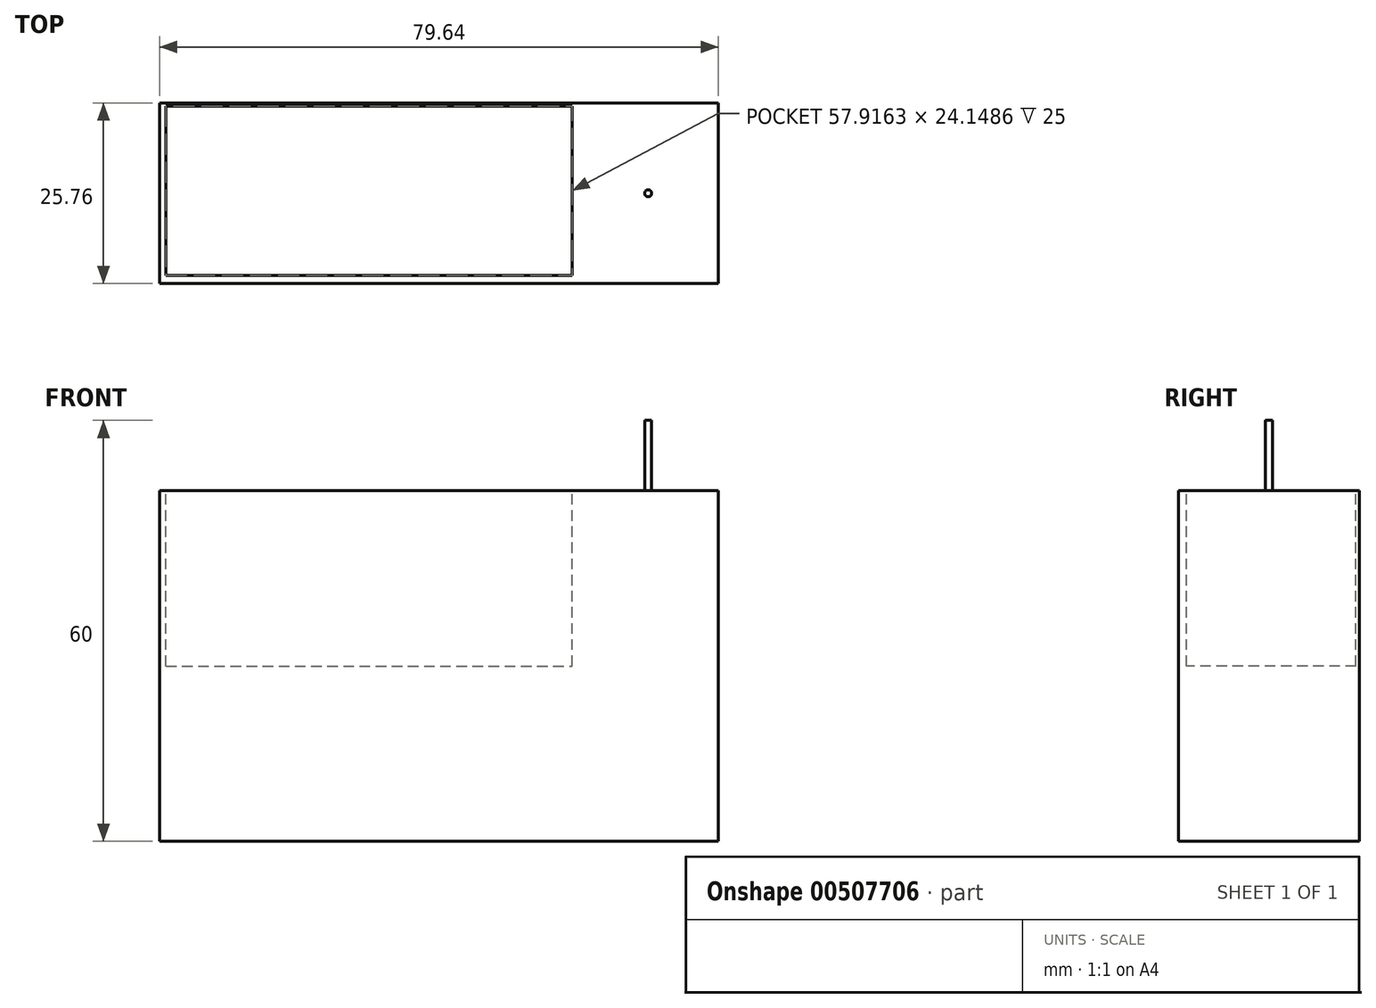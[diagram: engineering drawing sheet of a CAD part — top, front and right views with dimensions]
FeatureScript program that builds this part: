
annotation { "Feature Type Name" : "Feature", "Feature Type Description" : "" }
export const myFeature = defineFeature(function(context is Context, id is Id, definition is map)
    precondition{}
    {
        {
            var Q0;
            Q0=qCreatedBy(makeId("Top.planeOp"),FACE);
            var sketch = newSketch(context, id + "F0", { "sketchPlane" : qUnion([Q0])});
            skLineSegment(sketch, "E0.bottom", {"start": v(39.82, 12.88) * mm, "end": v(-39.82, 12.88) * mm});
            skLineSegment(sketch, "E0.top", {"start": v(39.82, -12.88) * mm, "end": v(-39.82, -12.88) * mm});
            skLineSegment(sketch, "E0.left", {"start": v(39.82, 12.88) * mm, "end": v(39.82, -12.88) * mm});
            skLineSegment(sketch, "E0.right", {"start": v(-39.82, 12.88) * mm, "end": v(-39.82, -12.88) * mm});
            skPoint(sketch, "E0.middle", {"position": v(0, 0) * mm});
            skSolve(sketch);
        }
        {
            var Q0;
            Q0=makeQuery(id+"F0.imprint","IMPRINT",FACE,{"disambiguationData":[TD([[makeQuery(id+"F0.imprint","IMPRINT",EDGE,{"derivedFrom":sQuery(id+"F0.wireOp",EDGE,"E0.bottom")}),1.0]])]});
            extrude(context, id + "F1", {"entities" : qUnion([Q0]), "depth" : 50 * mm});
        }
        {
            var Q0;
            Q0=makeQuery(id+"F1.opExtrude","CAP_FACE",FACE,{"disambiguationData":[OSD([sQuery(id+"F0.wireOp",EDGE,"E0.bottom"),sQuery(id+"F0.wireOp",EDGE,"E0.top"),sQuery(id+"F0.wireOp",EDGE,"E0.left"),sQuery(id+"F0.wireOp",EDGE,"E0.right")])],"isStart":false});
            var sketch = newSketch(context, id + "F2", { "sketchPlane" : qUnion([Q0])});
            skLineSegment(sketch, "E1.bottom", {"start": v(-38.91, 12.42) * mm, "end": v(19, 12.42) * mm});
            skLineSegment(sketch, "E1.top", {"start": v(-38.91, -11.73) * mm, "end": v(19, -11.73) * mm});
            skLineSegment(sketch, "E1.left", {"start": v(-38.91, 12.42) * mm, "end": v(-38.91, -11.73) * mm});
            skLineSegment(sketch, "E1.right", {"start": v(19, 12.42) * mm, "end": v(19, -11.73) * mm});
            skSolve(sketch);
        }
        {
            var Q0;
            Q0=makeQuery(id+"F2.imprint","IMPRINT",FACE,{"disambiguationData":[TD([[makeQuery(id+"F2.imprint","IMPRINT",EDGE,{"derivedFrom":sQuery(id+"F2.wireOp",EDGE,"E1.bottom")}),-1.0]])]});
            extrude(context, id + "F3", {"entities" : qUnion([Q0]), "operationType" : NewBodyOperationType.REMOVE, "oppositeDirection" : true, "depth" : 25 * mm});
        }
        {
            var Q0;
            Q0=makeQuery(id+"F1.opExtrude","CAP_FACE",FACE,{"disambiguationData":[OSD([sQuery(id+"F0.wireOp",EDGE,"E0.bottom"),sQuery(id+"F0.wireOp",EDGE,"E0.top"),sQuery(id+"F0.wireOp",EDGE,"E0.left"),sQuery(id+"F0.wireOp",EDGE,"E0.right")])],"isStart":false});
            var sketch = newSketch(context, id + "F4", { "sketchPlane" : qUnion([Q0])});
            skCircle(sketch, "E2", {"center": v(29.82, 0) * mm, "radius": 0.5 * mm});
            skSolve(sketch);
        }
        {
            var Q0;
            Q0=makeQuery(id+"F4.imprint","IMPRINT",FACE,{"disambiguationData":[TD([[makeQuery(id+"F4.imprint","IMPRINT",EDGE,{"derivedFrom":sQuery(id+"F4.wireOp",EDGE,"E2")}),1.0]])]});
            extrude(context, id + "F5", {"entities" : qUnion([Q0]), "operationType" : NewBodyOperationType.ADD, "depth" : 10 * mm});
        }
    });
